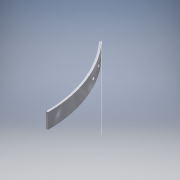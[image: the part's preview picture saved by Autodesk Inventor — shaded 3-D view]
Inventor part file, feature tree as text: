
AUTODESK INVENTOR PART (.ipt)
format: ipt  version: 2016 (Build 200138000, 138)  size: 120,320 bytes
history: native  units: in
note: dims shown in document units (in); Inventor stores cm internally (conversion verified against a paired STEP export)
features: extrude x2, sketch x2, plane x1
ambient origin geometry x8: Origin, YZ Plane, XZ Plane, XY Plane, X Axis, Y Axis, Z Axis, Center Point
bodies: Solid1 (feature_tree)
feature tree (5):
  extrude  "Extrusion1"  Depth=0.125in
  plane  "Work Plane1"
  extrude  "Extrusion2"  Depth=1.0in TaperAngle=0.0deg
  sketch  "Sketch1"  dims[d0=17.0in d1=0.125in]
  sketch  "Sketch2"  dims[d2=45.0deg d3=1.0in d4=0.0in d5=0.2656in d6=1.5in d7=0.2656in d8=0.75in d9=0.5in d10=0.5in d11=0.7in d12=0.0in]
